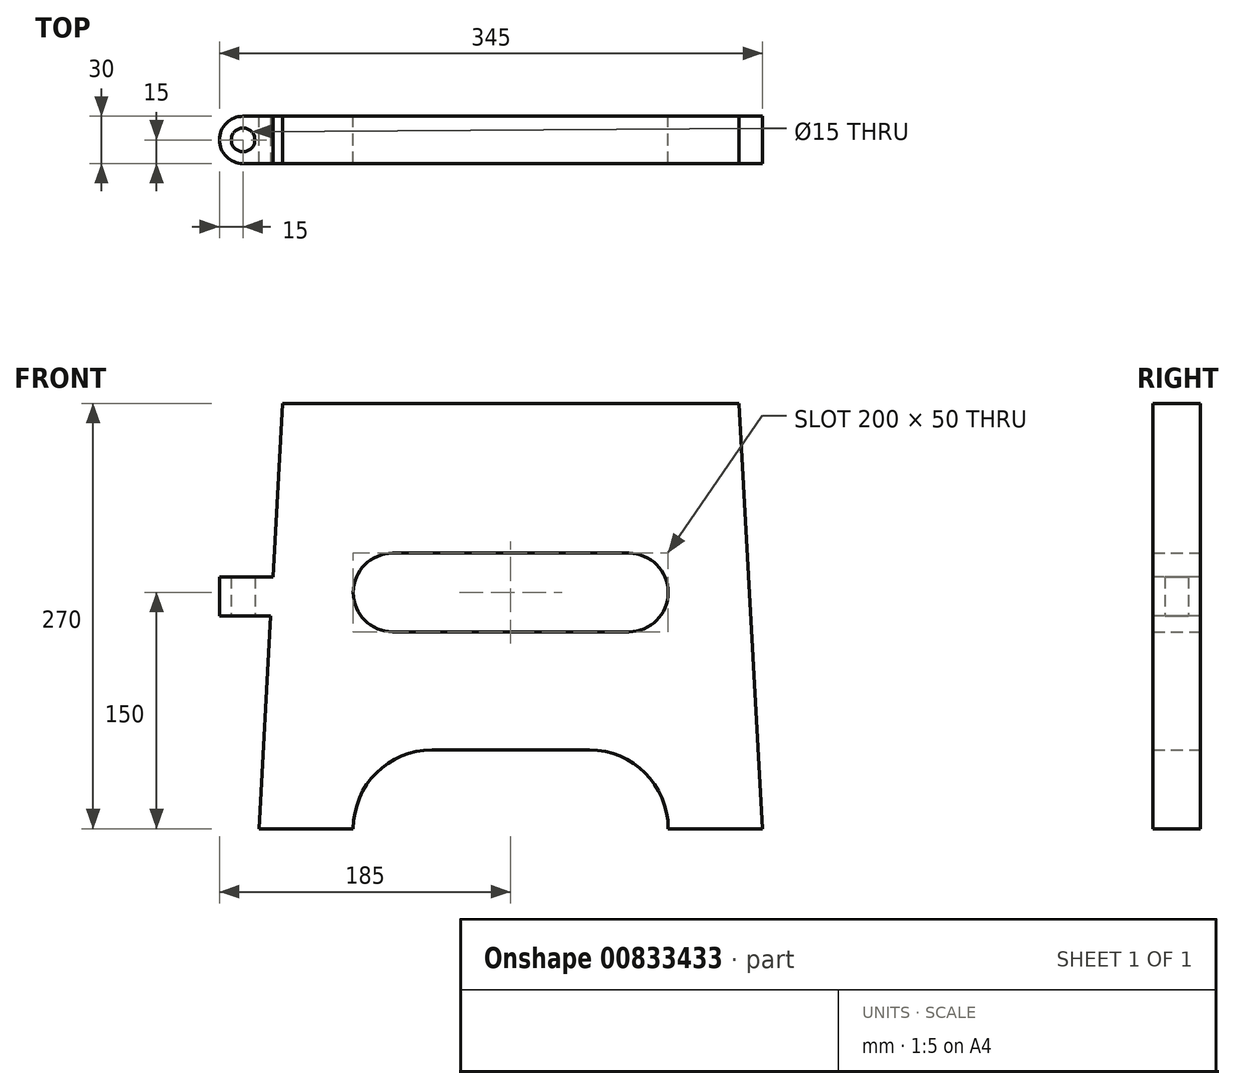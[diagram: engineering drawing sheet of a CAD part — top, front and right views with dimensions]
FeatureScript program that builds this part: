
annotation { "Feature Type Name" : "Feature", "Feature Type Description" : "" }
export const myFeature = defineFeature(function(context is Context, id is Id, definition is map)
    precondition{}
    {
        {
            var Q0;
            Q0=qCreatedBy(makeId("Front.planeOp"),FACE);
            var sketch = newSketch(context, id + "F0", { "sketchPlane" : qUnion([Q0])});
            skLineSegment(sketch, "E0", {"start": v(0, 270) * mm, "end": v(145, 270) * mm});
            skLineSegment(sketch, "E1", {"start": v(145, 270) * mm, "end": v(160, 0) * mm});
            skLineSegment(sketch, "E2", {"start": v(160, 0) * mm, "end": v(100, 0) * mm});
            skLineSegment(sketch, "E3", {"start": v(0, 270) * mm, "end": v(0, 0) * mm, "construction": true});
            skLineSegment(sketch, "E4", {"start": v(0, 50) * mm, "end": v(50, 50) * mm});
            skLineSegment(sketch, "E5", {"start": v(100, 0) * mm, "end": v(100, 0) * mm});
            skPoint(sketch, "E6.visualSharp", {"position": v(100, 50) * mm});
            skArc(sketch, "E6.filletArc", {"start": v(100, 0) * mm, "mid": v(85.36, 35.36) * mm, "end": v(50, 50) * mm});
            skLineSegment(sketch, "E7.MirrorCS", {"start": v(-160, 0) * mm, "end": v(-100, 0) * mm});
            skPoint(sketch, "E8.MirrorP", {"position": v(-100, 50) * mm});
            skArc(sketch, "E9.MirrorCS", {"start": v(-100, 0) * mm, "mid": v(-85.36, 35.36) * mm, "end": v(-50, 50) * mm});
            skLineSegment(sketch, "E10.MirrorCS", {"start": v(0, 270) * mm, "end": v(-145, 270) * mm});
            skLineSegment(sketch, "E11.MirrorCS", {"start": v(-145, 270) * mm, "end": v(-160, 0) * mm});
            skLineSegment(sketch, "E12.MirrorCS", {"start": v(0, 50) * mm, "end": v(-50, 50) * mm});
            skLineSegment(sketch, "E13.MirrorCS", {"start": v(-100, 0) * mm, "end": v(-100, 0) * mm});
            skArc(sketch, "E14", {"start": v(75, 125) * mm, "mid": v(100, 150) * mm, "end": v(75, 175) * mm});
            skLineSegment(sketch, "E15", {"start": v(75, 125) * mm, "end": v(0, 125) * mm});
            skLineSegment(sketch, "E16", {"start": v(75, 175) * mm, "end": v(0, 175) * mm});
            skArc(sketch, "E17.MirrorCS", {"start": v(-75, 125) * mm, "mid": v(-100, 150) * mm, "end": v(-75, 175) * mm});
            skLineSegment(sketch, "E18.MirrorCS", {"start": v(-75, 175) * mm, "end": v(0, 175) * mm});
            skLineSegment(sketch, "E19.MirrorCS", {"start": v(-75, 125) * mm, "end": v(0, 125) * mm});
            skSolve(sketch);
        }
        {
            var Q0;
            Q0 = qSketchRegion(id + "F0", true);
            extrude(context, id + "F1", {"entities" : qUnion([Q0]), "endBound" : BoundingType.SYMMETRIC, "depth" : 30 * mm, "offsetDistance" : 25 * mm});
        }
        {
            var Q0;
            Q0=qCreatedBy(makeId("Top.planeOp"),FACE);
            cPlane(context, id + "F2", {"entities" : qUnion([Q0]), "cplaneType" : CPlaneType.OFFSET, "offset" : 135 * mm, "width" : 150 * mm, "height" : 150 * mm});
        }
        {
            var Q0;
            Q0=qCreatedBy(id+"F2.planeOp",FACE);
            var sketch = newSketch(context, id + "F3", { "sketchPlane" : qUnion([Q0])});
            skArc(sketch, "E20", {"start": v(-170, 15) * mm, "mid": v(-185, 0) * mm, "end": v(-170, -15) * mm});
            skLineSegment(sketch, "E21", {"start": v(-170, -15) * mm, "end": v(-152.5, -15) * mm});
            skLineSegment(sketch, "E22", {"start": v(-152.5, 15) * mm, "end": v(-170, 15) * mm});
            skCircle(sketch, "E23", {"center": v(-170, 0) * mm, "radius": 7.5 * mm});
            skLineSegment(sketch, "E24", {"start": v(-152.5, 15) * mm, "end": v(-132.57, 15) * mm});
            skLineSegment(sketch, "E25", {"start": v(-132.57, 15) * mm, "end": v(-132.57, -15) * mm});
            skLineSegment(sketch, "E26", {"start": v(-132.57, -15) * mm, "end": v(-152.5, -15) * mm});
            skSolve(sketch);
        }
        {
            var Q0;
            Q0 = qSketchRegion(id + "F3", true);
            extrude(context, id + "F4", {"entities" : qUnion([Q0]), "operationType" : NewBodyOperationType.ADD, "depth" : 25 * mm, "offsetDistance" : 25 * mm});
        }
    });
